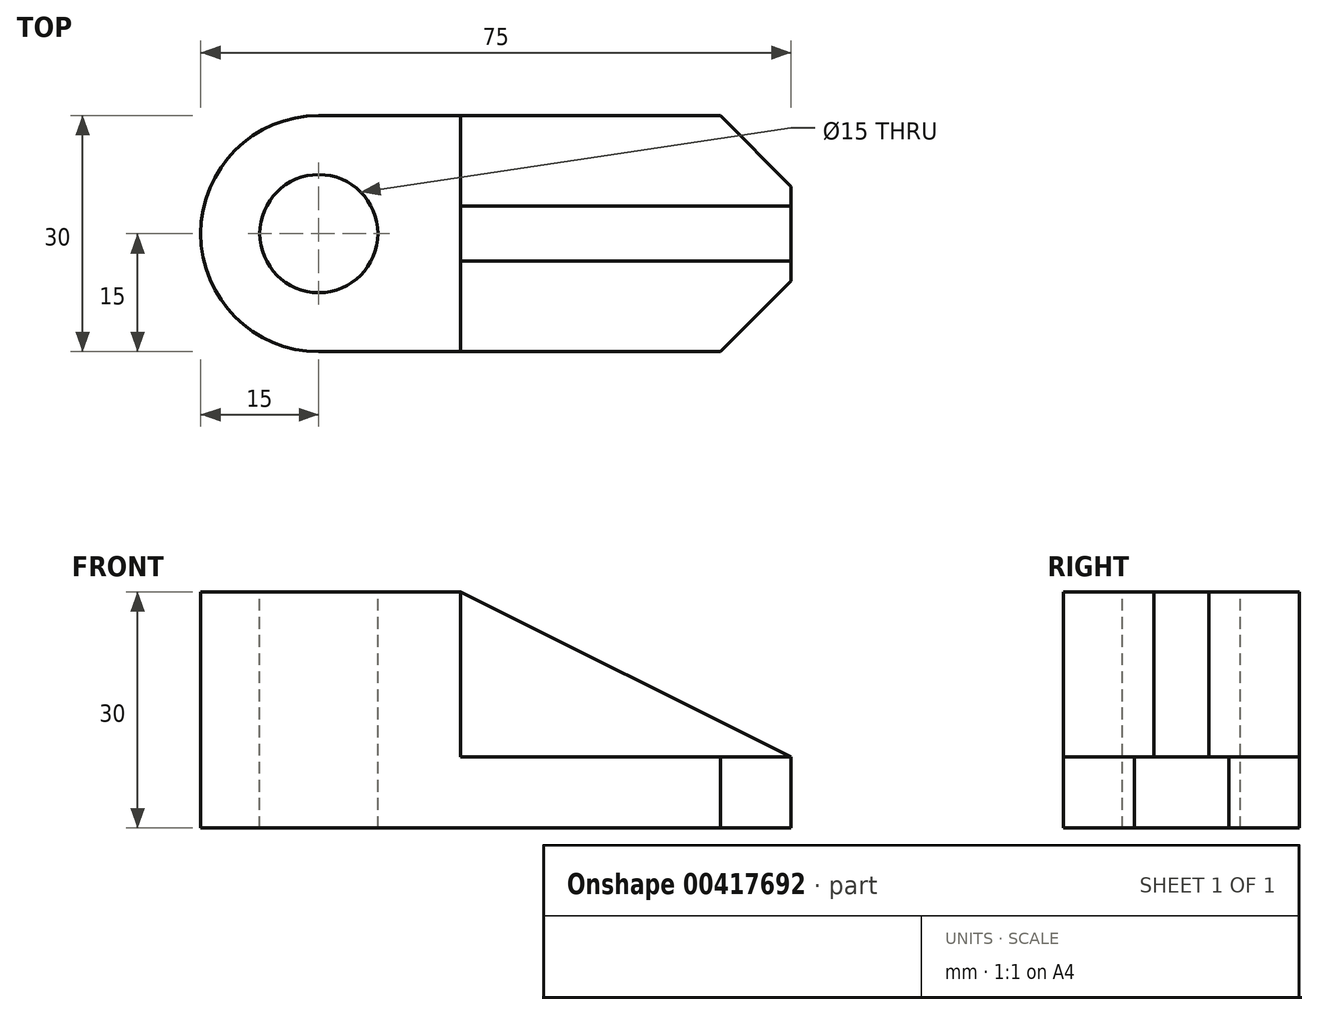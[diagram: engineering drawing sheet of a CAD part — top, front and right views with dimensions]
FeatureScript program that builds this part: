
annotation { "Feature Type Name" : "Feature", "Feature Type Description" : "" }
export const myFeature = defineFeature(function(context is Context, id is Id, definition is map)
    precondition{}
    {
        {
            var Q0;
            Q0=qCreatedBy(makeId("Top.planeOp"),FACE);
            var sketch = newSketch(context, id + "F0", { "sketchPlane" : qUnion([Q0])});
            skLineSegment(sketch, "E0.bottom", {"start": v(0, -15) * mm, "end": v(51, -15) * mm});
            skLineSegment(sketch, "E0.top", {"start": v(0, 15) * mm, "end": v(51, 15) * mm});
            skLineSegment(sketch, "E0.left", {"start": v(0, -15) * mm, "end": v(0, 15) * mm, "construction": true});
            skLineSegment(sketch, "E0.right", {"start": v(60, -6) * mm, "end": v(60, 6) * mm});
            skArc(sketch, "E1", {"start": v(0, 15) * mm, "mid": v(-15, 0) * mm, "end": v(0, -15) * mm});
            skLineSegment(sketch, "E2", {"start": v(51, 15) * mm, "end": v(60, 6) * mm});
            skLineSegment(sketch, "E3", {"start": v(60, -6) * mm, "end": v(51, -15) * mm});
            skSolve(sketch);
        }
        {
            var Q0;
            Q0=makeQuery(id+"F0.imprint","IMPRINT",FACE,{"disambiguationData":[TD([[makeQuery(id+"F0.imprint","IMPRINT",EDGE,{"derivedFrom":sQuery(id+"F0.wireOp",EDGE,"E0.bottom")}),1.0]])]});
            extrude(context, id + "F1", {"entities" : qUnion([Q0]), "depth" : 9 * mm});
        }
        {
            var Q0;
            Q0=makeQuery(id+"F1.opExtrude","CAP_FACE",FACE,{"disambiguationData":[OSD([sQuery(id+"F0.wireOp",EDGE,"E0.bottom"),sQuery(id+"F0.wireOp",EDGE,"E0.top"),sQuery(id+"F0.wireOp",EDGE,"E0.right"),sQuery(id+"F0.wireOp",EDGE,"E1"),sQuery(id+"F0.wireOp",EDGE,"E2"),sQuery(id+"F0.wireOp",EDGE,"E3")])],"isStart":false});
            var sketch = newSketch(context, id + "F2", { "sketchPlane" : qUnion([Q0])});
            skArc(sketch, "E4.0", {"start": v(0, 15) * mm, "mid": v(-15, 0) * mm, "end": v(0, -15) * mm});
            skLineSegment(sketch, "E5.bottom", {"start": v(0, 15) * mm, "end": v(18, 15) * mm});
            skLineSegment(sketch, "E5.top", {"start": v(0, -15) * mm, "end": v(18, -15) * mm});
            skLineSegment(sketch, "E5.left", {"start": v(0, 15) * mm, "end": v(0, -15) * mm, "construction": true});
            skLineSegment(sketch, "E5.right", {"start": v(18, 15) * mm, "end": v(18, -15) * mm});
            skSolve(sketch);
        }
        {
            var Q0;
            Q0=makeQuery(id+"F2.imprint","IMPRINT",FACE,{"disambiguationData":[TD([[makeQuery(id+"F2.imprint","IMPRINT",EDGE,{"derivedFrom":sQuery(id+"F2.wireOp",EDGE,"E4.0")}),1.0]])]});
            extrude(context, id + "F3", {"entities" : qUnion([Q0]), "operationType" : NewBodyOperationType.ADD, "depth" : 21 * mm});
        }
        {
            var Q0;
            Q0=makeQuery(id+"F1.opExtrude","CAP_FACE",FACE,{"disambiguationData":[OSD([sQuery(id+"F0.wireOp",EDGE,"E0.bottom"),sQuery(id+"F0.wireOp",EDGE,"E0.top"),sQuery(id+"F0.wireOp",EDGE,"E0.right"),sQuery(id+"F0.wireOp",EDGE,"E1"),sQuery(id+"F0.wireOp",EDGE,"E2"),sQuery(id+"F0.wireOp",EDGE,"E3")])],"isStart":false});
            var sketch = newSketch(context, id + "F4", { "sketchPlane" : qUnion([Q0])});
            skLineSegment(sketch, "E6.bottom", {"start": v(18, -3.5) * mm, "end": v(60, -3.5) * mm});
            skLineSegment(sketch, "E6.top", {"start": v(18, 3.5) * mm, "end": v(60, 3.5) * mm});
            skLineSegment(sketch, "E6.left", {"start": v(18, -3.5) * mm, "end": v(18, 3.5) * mm});
            skLineSegment(sketch, "E6.right", {"start": v(60, -3.5) * mm, "end": v(60, 3.5) * mm});
            skSolve(sketch);
        }
        {
            var Q0;
            Q0=sQuery(id+"F4.wireOp",EDGE,"E6.right");
            cPoint(context, id + "F5", {"entities" : qUnion([Q0]), "parameter" : 0.5});
        }
        {
            var Q0;
            Q0=makeQuery(id+"F3.opExtrude","CAP_VERTEX",VERTEX,{"disambiguationData":[OSD([sQuery(id+"F0.wireOp",EDGE,"E0.top"),sQuery(id+"F2.wireOp",EDGE,"E5.bottom"),sQuery(id+"F2.wireOp",EDGE,"E5.right")])],"isStart":false});
            var Q1;
            Q1=makeQuery(id+"F3.opExtrude","CAP_VERTEX",VERTEX,{"disambiguationData":[OSD([sQuery(id+"F0.wireOp",EDGE,"E0.bottom"),sQuery(id+"F2.wireOp",EDGE,"E5.top"),sQuery(id+"F2.wireOp",EDGE,"E5.right")])],"isStart":false});
            var Q2;
            Q2 = qCreatedBy(id + "F5" ,VERTEX);
            cPlane(context, id + "F6", {"entities" : qUnion([Q0, Q1, Q2]), "cplaneType" : CPlaneType.THREE_POINT, "offset" : 25 * mm, "width" : 150 * mm, "height" : 150 * mm});
        }
        {
            var Q0;
            Q0=makeQuery(id+"F4.imprint","IMPRINT",FACE,{"disambiguationData":[TD([[makeQuery(id+"F4.imprint","IMPRINT",EDGE,{"derivedFrom":sQuery(id+"F4.wireOp",EDGE,"E6.bottom")}),1.0]])]});
            var Q1;
            Q1=qCreatedBy(id+"F6.planeOp",FACE);
            extrude(context, id + "F7", {"entities" : qUnion([Q0]), "operationType" : NewBodyOperationType.ADD, "endBound" : BoundingType.UP_TO_SURFACE, "endBoundEntityFace" : qUnion([Q1]), "depth" : 25 * mm});
        }
        {
            var Q0;
            Q0=makeQuery(id+"F3.opExtrude","CAP_FACE",FACE,{"disambiguationData":[OSD([sQuery(id+"F2.wireOp",EDGE,"E4.0"),sQuery(id+"F2.wireOp",EDGE,"E5.bottom"),sQuery(id+"F2.wireOp",EDGE,"E5.top"),sQuery(id+"F2.wireOp",EDGE,"E5.right")])],"isStart":false});
            var sketch = newSketch(context, id + "F8", { "sketchPlane" : qUnion([Q0])});
            skCircle(sketch, "E7", {"center": v(0, 0) * mm, "radius": 7.5 * mm});
            skSolve(sketch);
        }
        {
            var Q0;
            Q0=makeQuery(id+"F8.imprint","IMPRINT",FACE,{"disambiguationData":[TD([[makeQuery(id+"F8.imprint","IMPRINT",EDGE,{"derivedFrom":sQuery(id+"F8.wireOp",EDGE,"E7")}),1.0]])]});
            extrude(context, id + "F9", {"entities" : qUnion([Q0]), "operationType" : NewBodyOperationType.REMOVE, "endBound" : BoundingType.THROUGH_ALL, "oppositeDirection" : true, "depth" : 25 * mm});
        }
    });
